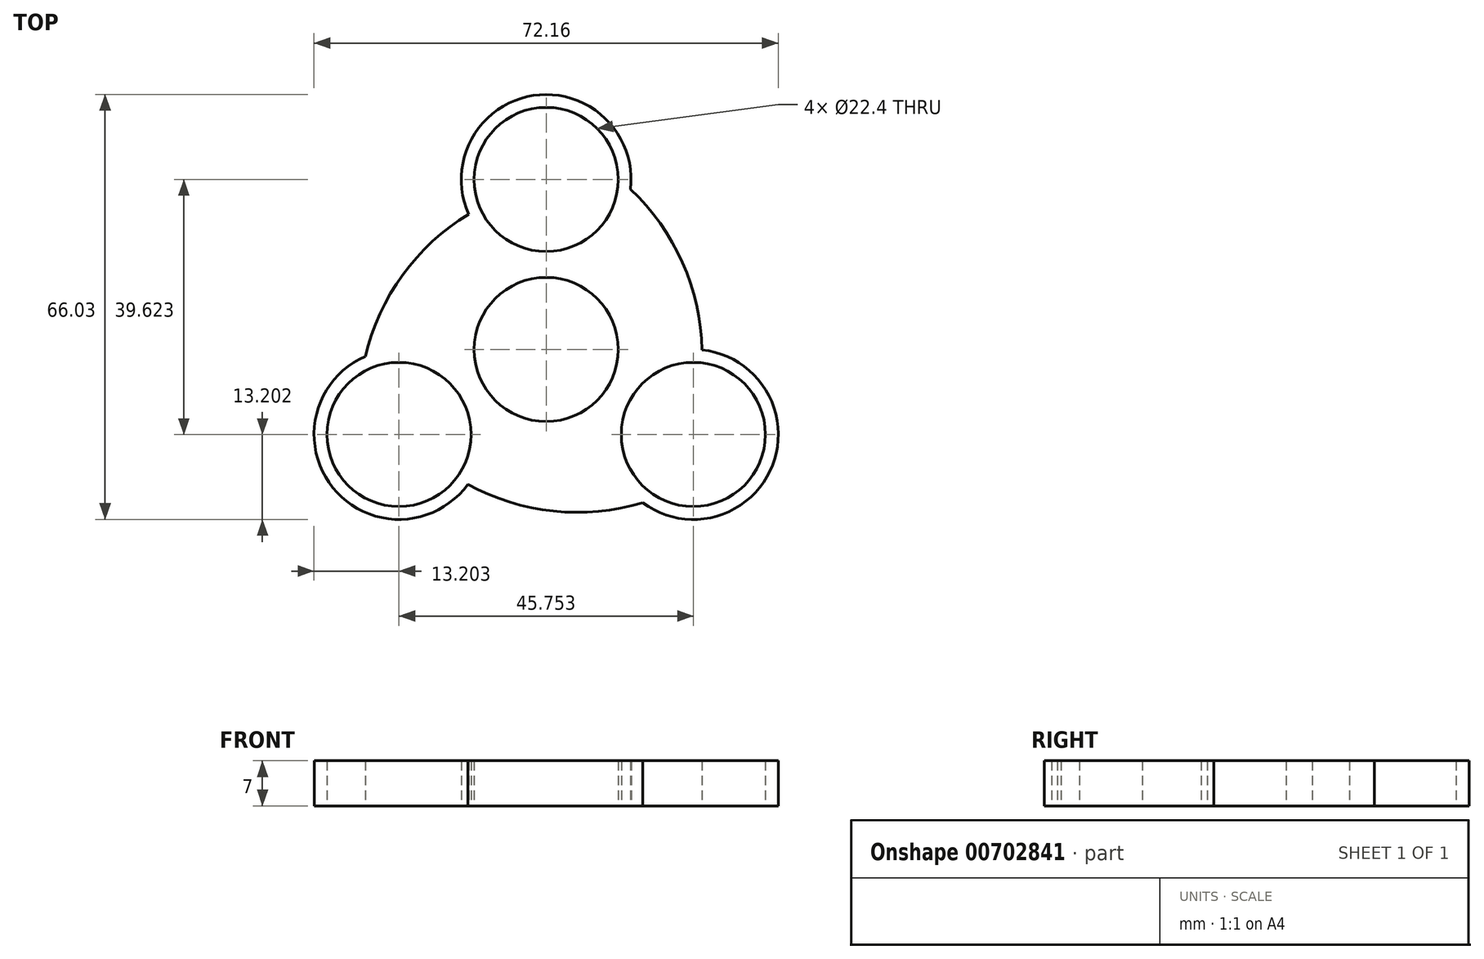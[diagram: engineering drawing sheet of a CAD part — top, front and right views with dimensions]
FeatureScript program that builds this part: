
annotation { "Feature Type Name" : "Feature", "Feature Type Description" : "" }
export const myFeature = defineFeature(function(context is Context, id is Id, definition is map)
    precondition{}
    {
        {
            var Q0;
            Q0=qCreatedBy(makeId("Top.planeOp"),FACE);
            var sketch = newSketch(context, id + "F0", { "sketchPlane" : qUnion([Q0])});
            skCircle(sketch, "E0", {"center": v(0, 0) * mm, "radius": 11.2 * mm});
            skCircle(sketch, "E1", {"center": v(0, 26.42) * mm, "radius": 11.2 * mm});
            skArc(sketch, "E2", {"start": v(13.11, 24.91) * mm, "mid": v(-2.01, 39.46) * mm, "end": v(-12.05, 21.03) * mm});
            skArc(sketch, "E3.1.0", {"start": v(-28.13, -1.1) * mm, "mid": v(-33.17, -21.47) * mm, "end": v(-12.19, -20.95) * mm});
            skArc(sketch, "E3.2.0", {"start": v(15.02, -23.81) * mm, "mid": v(35.18, -17.99) * mm, "end": v(24.24, -0.08) * mm});
            skArc(sketch, "E4", {"start": v(24.24, -0.08) * mm, "mid": v(21.19, 13.53) * mm, "end": v(13.11, 24.91) * mm});
            skArc(sketch, "E5.1.0", {"start": v(-12.05, 21.03) * mm, "mid": v(-22.31, 11.58) * mm, "end": v(-28.13, -1.1) * mm});
            skArc(sketch, "E5.2.0", {"start": v(-12.19, -20.95) * mm, "mid": v(1.13, -25.11) * mm, "end": v(15.02, -23.81) * mm});
            skCircle(sketch, "E6.1.0", {"center": v(-22.88, -13.2) * mm, "radius": 11.2 * mm});
            skCircle(sketch, "E6.2.0", {"center": v(22.88, -13.2) * mm, "radius": 11.2 * mm});
            skSolve(sketch);
        }
        {
            var Q0;
            Q0 = qSketchRegion(id + "F0", true);
            extrude(context, id + "F1", {"entities" : qUnion([Q0]), "depth" : 7 * mm, "offsetDistance" : 25 * mm});
        }
    });
